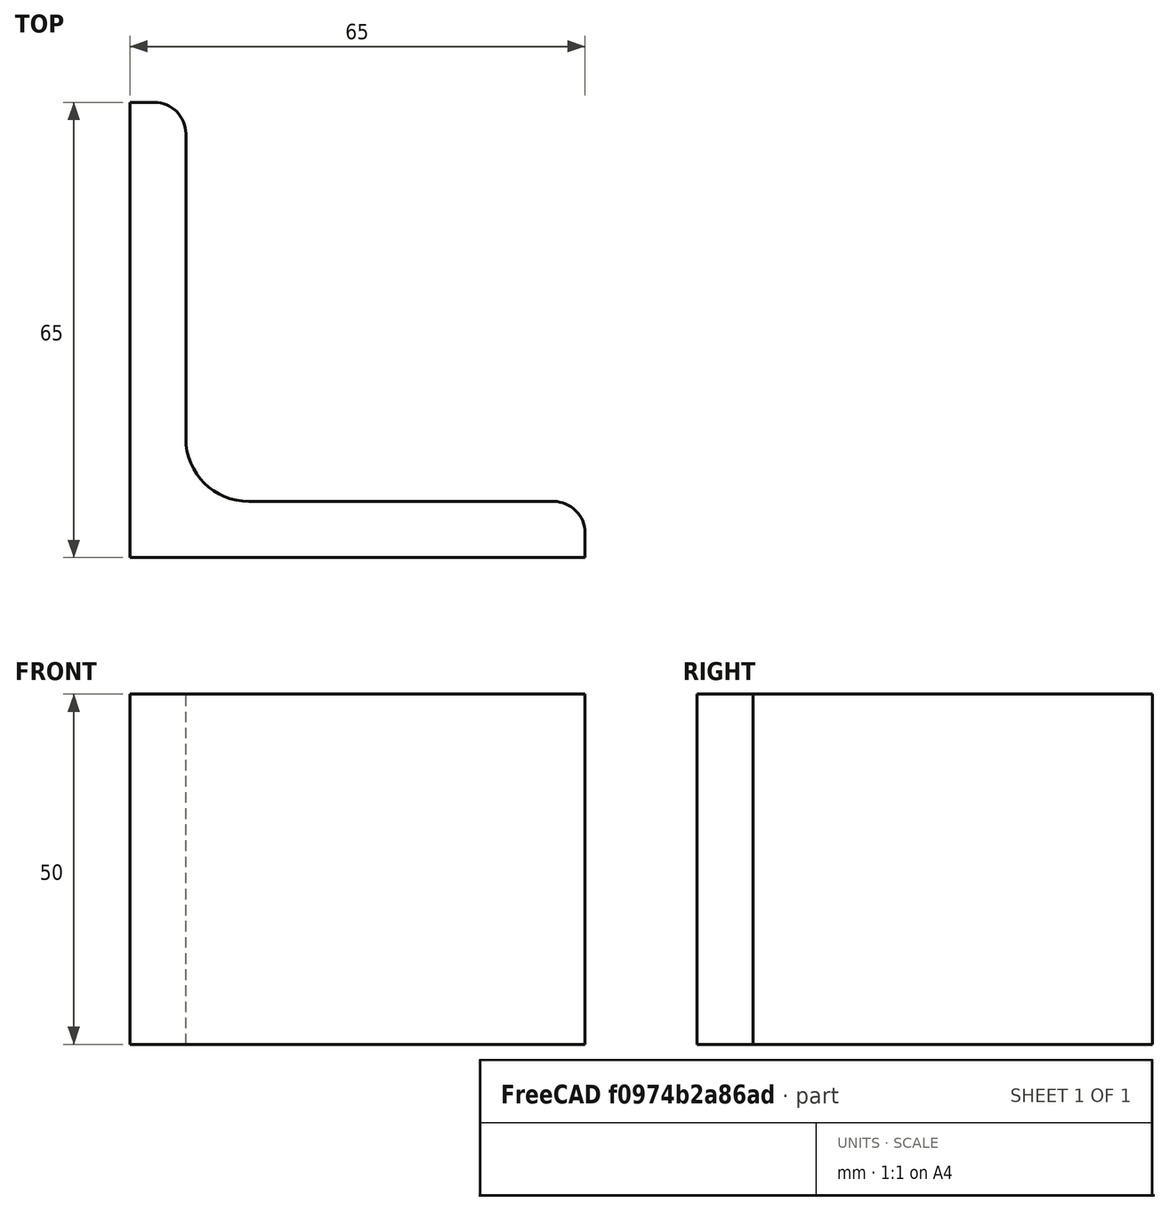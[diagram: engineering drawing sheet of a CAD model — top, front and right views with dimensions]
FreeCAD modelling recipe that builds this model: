
FCSTD DOCUMENT  (FreeCAD 0.15R4671 (Git))
Label: Angle Bar L65x65x8 EN10056 S235JR
License: All rights reserved
LicenseURL: http://en.wikipedia.org/wiki/All_rights_reserved
objects: Sketcher::SketchObject×1, Part::Extrusion×1
note: 2 computed .brp shape members not serialized (recipe doc carries the construction recipe); baked Part::Feature solids carry a one-line shape summary decoded from their .brp

FEATURE [Sketcher::SketchObject] Sketch
  sketch-geometry (9):
    g0: LineSegment StartX=0 StartY=0 StartZ=0 EndX=65 EndY=0 EndZ=0
    g1: LineSegment StartX=65 StartY=0 StartZ=0 EndX=65 EndY=3.5 EndZ=0
    g2: LineSegment StartX=60.5 StartY=8 StartZ=0 EndX=17 EndY=8 EndZ=0
    g3: LineSegment StartX=0 StartY=0 StartZ=0 EndX=0 EndY=65 EndZ=0
    g4: LineSegment StartX=0 StartY=65 StartZ=0 EndX=3.5 EndY=65 EndZ=0
    g5: LineSegment StartX=8 StartY=60.5 StartZ=0 EndX=8 EndY=17 EndZ=0
    g6: ArcOfCircle CenterX=17 CenterY=17 CenterZ=0 NormalX=0 NormalY=0 NormalZ=1 Radius=9 StartAngle=3.14159 EndAngle=4.71239
    g7: ArcOfCircle CenterX=3.5 CenterY=60.5 CenterZ=0 NormalX=0 NormalY=0 NormalZ=1 Radius=4.5 StartAngle=0 EndAngle=1.5708
    g8: ArcOfCircle CenterX=60.5 CenterY=3.5 CenterZ=0 NormalX=0 NormalY=0 NormalZ=1 Radius=4.5 StartAngle=0 EndAngle=1.5708
  constraints (23):
    c: Coincident(g0,g-1)
    c: Horizontal(g0)
    c: Coincident(g1,g0)
    c: Vertical(g1)
    c: Horizontal(g2)
    c: Coincident(g3,g-1)
    c: Vertical(g3)
    c: Coincident(g4,g3)
    c: Horizontal(g4)
    c: Vertical(g5)
    c: Tangent(g5,g6) = -1.5708
    c: Tangent(g2,g6) = 1.5708
    c: Tangent(g4,g7) = 1.5708
    c: Tangent(g5,g7) = 1.5708
    c: Tangent(g2,g8) = -1.5708
    c: Tangent(g1,g8) = -1.5708
    c: DistanceX(g0) = 65
    c: DistanceY(g3) = 65
    c: DistanceY(g0,g2) = 8
    c: DistanceX(g3,g5) = 8
    c: Radius(g6) = 9
    c: Radius(g8) = 4.5
    c: Radius(g7) = 4.5
FEATURE [Part::Extrusion] Extrude  label="Angle Bar L65x65x8 EN10056 S235JR"
  Base = -> Sketch
  Dir = (0,0,50)
  Solid = true
